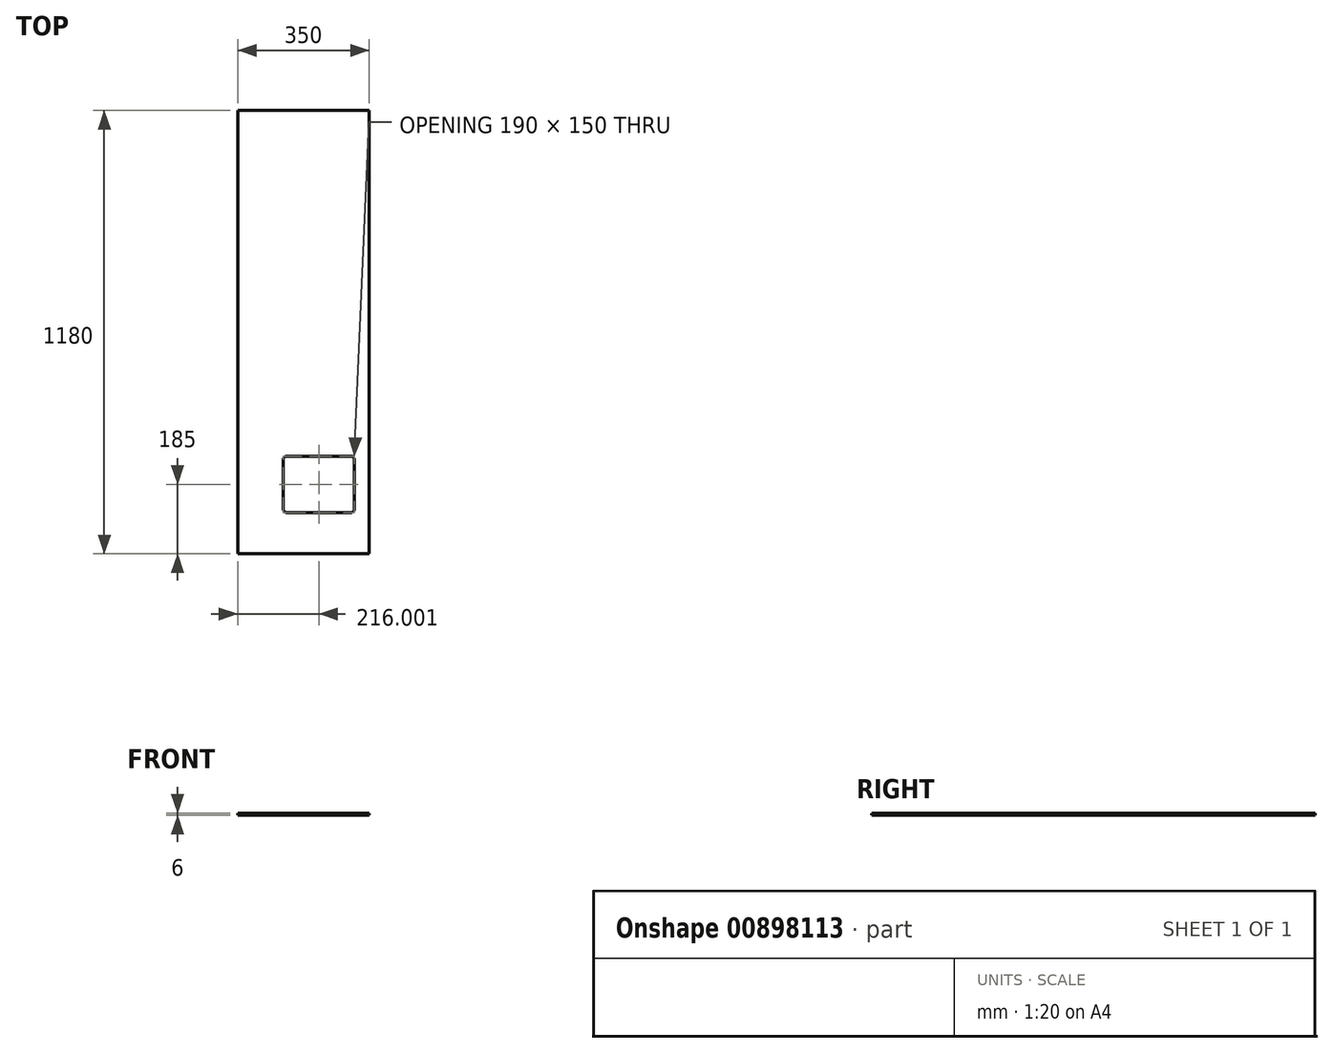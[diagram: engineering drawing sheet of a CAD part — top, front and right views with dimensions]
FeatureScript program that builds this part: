
annotation { "Feature Type Name" : "Feature", "Feature Type Description" : "" }
export const myFeature = defineFeature(function(context is Context, id is Id, definition is map)
    precondition{}
    {
        {
            var Q0;
            Q0=qCreatedBy(makeId("Front.planeOp"),FACE);
            var sketch = newSketch(context, id + "F0", { "sketchPlane" : qUnion([Q0])});
            skLineSegment(sketch, "E0.bottom", {"start": v(0, 0) * mm, "end": v(350, 0) * mm});
            skLineSegment(sketch, "E0.top", {"start": v(0, 6) * mm, "end": v(350, 6) * mm});
            skLineSegment(sketch, "E0.left", {"start": v(0, 0) * mm, "end": v(0, 6) * mm});
            skLineSegment(sketch, "E0.right", {"start": v(350, 0) * mm, "end": v(350, 6) * mm});
            skSolve(sketch);
        }
        {
            var Q0;
            Q0=qSketchRegion(id+"F0",true);
            extrude(context, id + "F1", {"entities" : qUnion([Q0]), "depth" : 1180 * mm, "offsetDistance" : 25 * mm});
        }
        {
            var Q0;
            Q0=makeQuery(id+"F1.opExtrude","SWEPT_FACE",FACE,{"disambiguationData":[OSD([sQuery(id+"F0.wireOp",EDGE,"E0.top")])]});
            var sketch = newSketch(context, id + "F2", { "sketchPlane" : qUnion([Q0])});
            skPoint(sketch, "E1", {"position": v(313.8, -995) * mm});
            skPoint(sketch, "E2", {"position": v(311, -995) * mm});
            skLineSegment(sketch, "E3", {"start": v(311, -995) * mm, "end": v(311, -930) * mm});
            skLineSegment(sketch, "E4", {"start": v(311, -995) * mm, "end": v(311, -1060) * mm});
            skPoint(sketch, "E5", {"position": v(350, -1076.19) * mm});
            skLineSegment(sketch, "E6", {"start": v(131, -1070) * mm, "end": v(301, -1070) * mm});
            skLineSegment(sketch, "E7", {"start": v(121, -1060) * mm, "end": v(121, -930) * mm});
            skLineSegment(sketch, "E8", {"start": v(131, -920) * mm, "end": v(301, -920) * mm});
            skPoint(sketch, "E9.visualSharp", {"position": v(121, -1070) * mm});
            skArc(sketch, "E9.filletArc", {"start": v(121, -1060) * mm, "mid": v(123.93, -1067.07) * mm, "end": v(131, -1070) * mm});
            skPoint(sketch, "E10.visualSharp", {"position": v(121, -920) * mm});
            skArc(sketch, "E10.filletArc", {"start": v(131, -920) * mm, "mid": v(123.93, -922.93) * mm, "end": v(121, -930) * mm});
            skPoint(sketch, "E11.visualSharp", {"position": v(311, -920) * mm});
            skArc(sketch, "E11.filletArc", {"start": v(311, -930) * mm, "mid": v(308.07, -922.93) * mm, "end": v(301, -920) * mm});
            skPoint(sketch, "E12.visualSharp", {"position": v(311, -1070) * mm});
            skArc(sketch, "E12.filletArc", {"start": v(301, -1070) * mm, "mid": v(308.07, -1067.07) * mm, "end": v(311, -1060) * mm});
            skSolve(sketch);
        }
        {
            var Q0;
            Q0=makeQuery(id+"F2.imprint","IMPRINT",FACE,{"disambiguationData":[TD([[makeQuery(id+"F2.imprint","IMPRINT",EDGE,{"derivedFrom":sQuery(id+"F2.wireOp",EDGE,"E3")}),1.0]])]});
            extrude(context, id + "F3", {"entities" : qUnion([Q0]), "operationType" : NewBodyOperationType.REMOVE, "oppositeDirection" : true, "depth" : 6 * mm, "offsetDistance" : 25 * mm});
        }
    });
